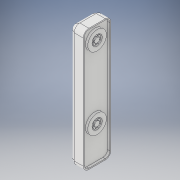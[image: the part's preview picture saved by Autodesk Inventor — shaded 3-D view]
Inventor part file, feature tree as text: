
AUTODESK INVENTOR PART (.ipt)
format: ipt  version: 2019 (Build 230136000, 136)  size: 887,808 bytes
history: native  units: mm
features: sketch x1, projected_geometry x1
ambient origin geometry x8: Origin, YZ Plane, XZ Plane, XY Plane, X Axis, Y Axis, Z Axis, Center Point
bodies: body (feature_tree), Solid1 (feature_tree)
feature tree (2):
  sketch  "Sketch1"
  projected_geometry  "Projected Loop1"
